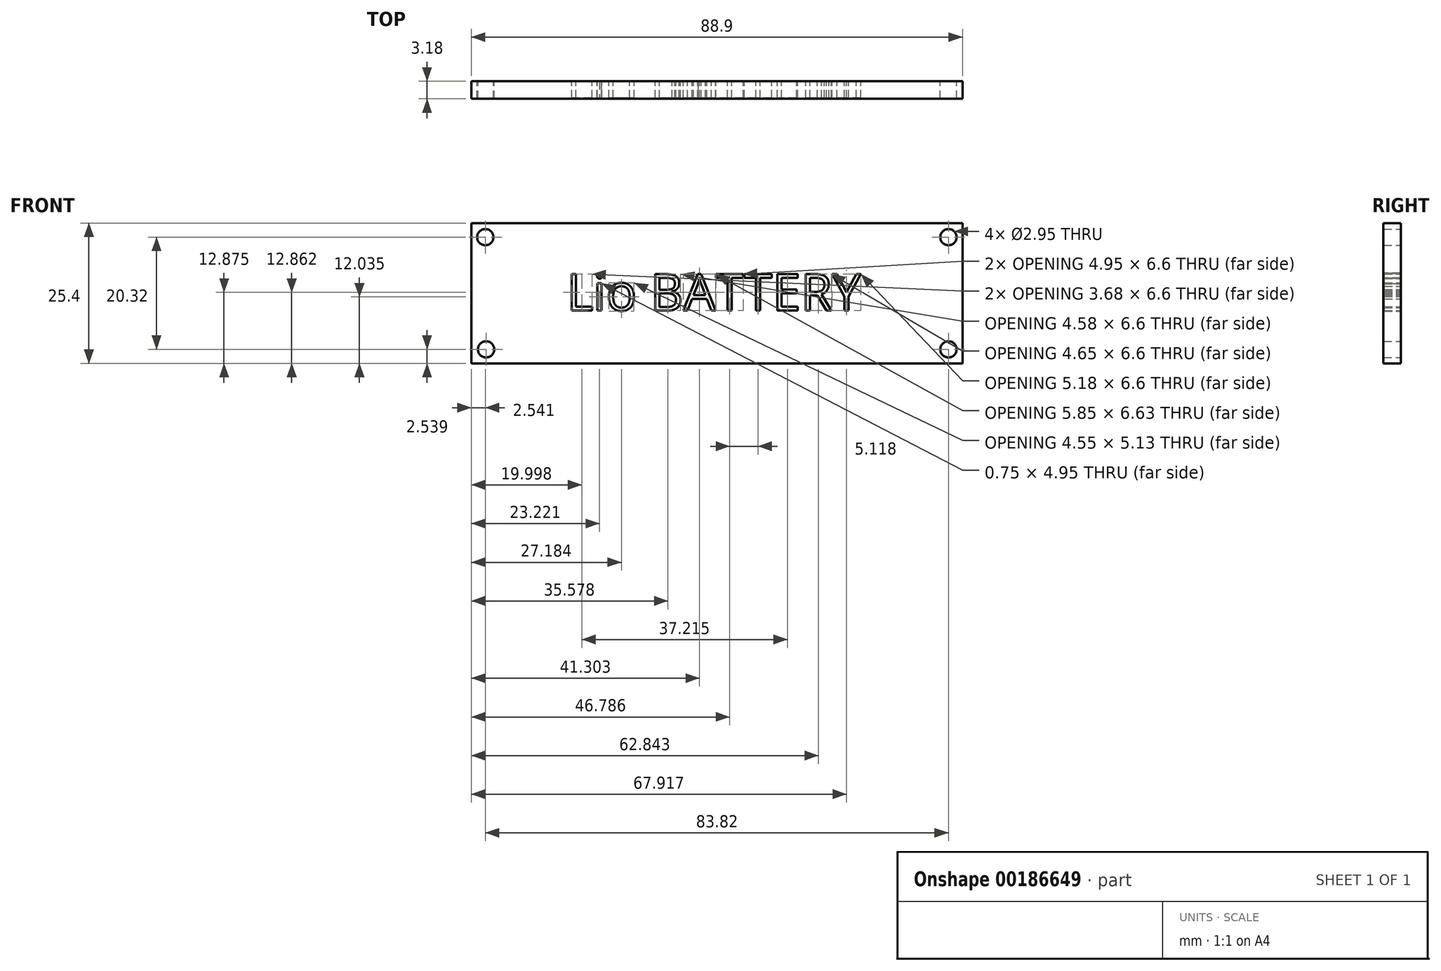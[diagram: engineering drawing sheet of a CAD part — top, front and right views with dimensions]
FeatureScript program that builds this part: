
annotation { "Feature Type Name" : "Feature", "Feature Type Description" : "" }
export const myFeature = defineFeature(function(context is Context, id is Id, definition is map)
    precondition{}
    {
        {
            var Q0;
            Q0=qCreatedBy(makeId("Front.planeOp"),FACE);
            var sketch = newSketch(context, id + "F0", { "sketchPlane" : qUnion([Q0])});
            skLineSegment(sketch, "E0", {"start": v(-37, 26.19) * mm, "end": v(51.9, 26.19) * mm});
            skLineSegment(sketch, "E1", {"start": v(-37, 26.19) * mm, "end": v(-37, 0.79) * mm});
            skLineSegment(sketch, "E2", {"start": v(-37, 0.79) * mm, "end": v(51.9, 0.79) * mm});
            skLineSegment(sketch, "E3", {"start": v(51.9, 0.79) * mm, "end": v(51.9, 26.19) * mm});
            skCircle(sketch, "E4", {"center": v(-34.47, 23.65) * mm, "radius": 1.47 * mm});
            skCircle(sketch, "E5", {"center": v(-34.33, 3.33) * mm, "radius": 1.47 * mm});
            skCircle(sketch, "E6", {"center": v(49.35, 3.33) * mm, "radius": 1.47 * mm});
            skCircle(sketch, "E7", {"center": v(49.35, 23.65) * mm, "radius": 1.47 * mm});
            skText(sketch, "E8", { "text": "Lio BATTERY", "fontName": "OpenSans-Regular.ttf"});
            skLineSegment(sketch, "E9", {"start": v(51.9, 26.19) * mm, "end": v(-37, 0.79) * mm, "construction": true});
            skLineSegment(sketch, "E10", {"start": v(-37, 26.19) * mm, "end": v(51.9, 0.79) * mm, "construction": true});
            skLineSegment(sketch, "E11", {"start": v(-27.3, 26.19) * mm, "end": v(-27.3, 22.63) * mm, "construction": true});
            skLineSegment(sketch, "E12", {"start": v(-37, 18.2) * mm, "end": v(-33.45, 18.2) * mm, "construction": true});
            skLineSegment(sketch, "E13", {"start": v(-26.7, 0.79) * mm, "end": v(-26.7, 4.35) * mm, "construction": true});
            skLineSegment(sketch, "E14", {"start": v(51.9, 20.21) * mm, "end": v(48.34, 20.21) * mm, "construction": true});
            skLineSegment(sketch, "E15.top", {"start": v(-31.92, 2.35) * mm, "end": v(46.82, 2.35) * mm});
            skLineSegment(sketch, "E16.top", {"start": v(-35.41, 21.08) * mm, "end": v(-34.46, 21.08) * mm});
            skLineSegment(sketch, "E16.right", {"start": v(-31.92, 24.57) * mm, "end": v(-31.92, 23.62) * mm});
            skArc(sketch, "E17.filletArc", {"start": v(-34.46, 21.08) * mm, "mid": v(-32.66, 21.82) * mm, "end": v(-31.92, 23.62) * mm});
            skLineSegment(sketch, "E18.trimOffspring", {"start": v(-31.92, 24.57) * mm, "end": v(46.82, 24.57) * mm});
            skLineSegment(sketch, "E19.trimOffspring", {"start": v(-35.41, 21.08) * mm, "end": v(-35.41, 5.84) * mm});
            skLineSegment(sketch, "E20.top", {"start": v(50.31, 21.08) * mm, "end": v(49.36, 21.08) * mm});
            skLineSegment(sketch, "E20.right", {"start": v(46.82, 24.57) * mm, "end": v(46.82, 23.62) * mm});
            skArc(sketch, "E21.filletArc", {"start": v(46.82, 23.62) * mm, "mid": v(47.57, 21.82) * mm, "end": v(49.36, 21.08) * mm});
            skLineSegment(sketch, "E22.top", {"start": v(50.31, 5.84) * mm, "end": v(49.36, 5.84) * mm});
            skArc(sketch, "E23.filletArc", {"start": v(49.36, 5.84) * mm, "mid": v(47.6, 5.14) * mm, "end": v(46.82, 3.42) * mm});
            skLineSegment(sketch, "E24.top", {"start": v(-35.41, 5.84) * mm, "end": v(-34.46, 5.84) * mm});
            skLineSegment(sketch, "E24.right", {"start": v(-31.92, 2.35) * mm, "end": v(-31.92, 3.3) * mm});
            skArc(sketch, "E25.filletArc", {"start": v(-31.92, 3.3) * mm, "mid": v(-32.66, 5.1) * mm, "end": v(-34.46, 5.84) * mm});
            skLineSegment(sketch, "E26", {"start": v(-35.42, 19.5) * mm, "end": v(-37, 19.5) * mm, "construction": true});
            skLineSegment(sketch, "E27", {"start": v(46.82, 3.42) * mm, "end": v(46.82, 2.35) * mm});
            skLineSegment(sketch, "E28", {"start": v(46.82, 2.35) * mm, "end": v(46.82, 0.76) * mm, "construction": true});
            skLineSegment(sketch, "E29", {"start": v(50.31, 21.08) * mm, "end": v(50.31, 5.84) * mm});
            const initialGuessF0  = {"E8": [-0.01976, 0.01035, 1, 0, 0.00666]};
            skSetInitialGuess(sketch, initialGuessF0);
            skSolve(sketch);
        }
        {
            var Q0;
            Q0=makeQuery(id+"F0.imprint","IMPRINT",FACE,{"disambiguationData":[TD([[makeQuery(id+"F0.imprint","IMPRINT",EDGE,{"derivedFrom":sQuery(id+"F0.wireOp",EDGE,"E0")}),-1.0]])]});
            var Q1;
            Q1=makeQuery(id+"F0.imprint","IMPRINT",FACE,{"disambiguationData":[TD([[makeQuery(id+"F0.imprint","IMPRINT",EDGE,{"derivedFrom":sQuery(id+"F0.wireOp",EDGE,"E8.sketch_text.stroke-27")}),1.0]])]});
            var Q2;
            Q2=makeQuery(id+"F0.imprint","IMPRINT",FACE,{"disambiguationData":[TD([[makeQuery(id+"F0.imprint","IMPRINT",EDGE,{"derivedFrom":sQuery(id+"F0.wireOp",EDGE,"E8.sketch_text.stroke-46")}),1.0]])]});
            var Q3;
            Q3=makeQuery(id+"F0.imprint","IMPRINT",FACE,{"disambiguationData":[TD([[makeQuery(id+"F0.imprint","IMPRINT",EDGE,{"derivedFrom":sQuery(id+"F0.wireOp",EDGE,"E8.sketch_text.stroke-53")}),1.0]])]});
            var Q4;
            Q4=makeQuery(id+"F0.imprint","IMPRINT",FACE,{"disambiguationData":[TD([[makeQuery(id+"F0.imprint","IMPRINT",EDGE,{"derivedFrom":sQuery(id+"F0.wireOp",EDGE,"E8.sketch_text.stroke-68")}),1.0]])]});
            var Q5;
            Q5=makeQuery(id+"F0.imprint","IMPRINT",FACE,{"disambiguationData":[TD([[makeQuery(id+"F0.imprint","IMPRINT",EDGE,{"derivedFrom":sQuery(id+"F0.wireOp",EDGE,"E8.sketch_text.stroke-112")}),1.0]])]});
            var Q6;
            Q6=makeQuery(id+"F0.imprint","IMPRINT",FACE,{"disambiguationData":[TD([[makeQuery(id+"F0.imprint","IMPRINT",EDGE,{"derivedFrom":sQuery(id+"F0.wireOp",EDGE,"E8.sketch_text.stroke-0")}),1.0]])]});
            extrude(context, id + "F1", {"entities" : qUnion([Q0, Q1, Q2, Q3, Q4, Q5, Q6]), "depth" : 3.17 * mm});
        }
        {
            var Q0;
            Q0=makeQuery(id+"F0.imprint","IMPRINT",FACE,{"disambiguationData":[TD([[makeQuery(id+"F0.imprint","IMPRINT",EDGE,{"derivedFrom":sQuery(id+"F0.wireOp",EDGE,"E8.sketch_text.stroke-0")}),-1.0]])]});
            var Q1;
            Q1=makeQuery(id+"F0.imprint","IMPRINT",FACE,{"disambiguationData":[TD([[makeQuery(id+"F0.imprint","IMPRINT",EDGE,{"derivedFrom":sQuery(id+"F0.wireOp",EDGE,"E8.sketch_text.stroke-6")}),-1.0]])]});
            var Q2;
            Q2=makeQuery(id+"F0.imprint","IMPRINT",FACE,{"disambiguationData":[TD([[makeQuery(id+"F0.imprint","IMPRINT",EDGE,{"derivedFrom":sQuery(id+"F0.wireOp",EDGE,"E8.sketch_text.stroke-10")}),-1.0]])]});
            var Q3;
            Q3=makeQuery(id+"F0.imprint","IMPRINT",FACE,{"disambiguationData":[TD([[makeQuery(id+"F0.imprint","IMPRINT",EDGE,{"derivedFrom":sQuery(id+"F0.wireOp",EDGE,"E8.sketch_text.stroke-18")}),-1.0]])]});
            var Q4;
            Q4=makeQuery(id+"F0.imprint","IMPRINT",FACE,{"disambiguationData":[TD([[makeQuery(id+"F0.imprint","IMPRINT",EDGE,{"derivedFrom":sQuery(id+"F0.wireOp",EDGE,"E8.sketch_text.stroke-35")}),-1.0]])]});
            var Q5;
            Q5=makeQuery(id+"F0.imprint","IMPRINT",FACE,{"disambiguationData":[TD([[makeQuery(id+"F0.imprint","IMPRINT",EDGE,{"derivedFrom":sQuery(id+"F0.wireOp",EDGE,"E8.sketch_text.stroke-60")}),-1.0]])]});
            var Q6;
            Q6=makeQuery(id+"F0.imprint","IMPRINT",FACE,{"disambiguationData":[TD([[makeQuery(id+"F0.imprint","IMPRINT",EDGE,{"derivedFrom":sQuery(id+"F0.wireOp",EDGE,"E8.sketch_text.stroke-73")}),-1.0]])]});
            var Q7;
            Q7=makeQuery(id+"F0.imprint","IMPRINT",FACE,{"disambiguationData":[TD([[makeQuery(id+"F0.imprint","IMPRINT",EDGE,{"derivedFrom":sQuery(id+"F0.wireOp",EDGE,"E8.sketch_text.stroke-81")}),-1.0]])]});
            var Q8;
            Q8=makeQuery(id+"F0.imprint","IMPRINT",FACE,{"disambiguationData":[TD([[makeQuery(id+"F0.imprint","IMPRINT",EDGE,{"derivedFrom":sQuery(id+"F0.wireOp",EDGE,"E8.sketch_text.stroke-89")}),-1.0]])]});
            var Q9;
            Q9=makeQuery(id+"F0.imprint","IMPRINT",FACE,{"disambiguationData":[TD([[makeQuery(id+"F0.imprint","IMPRINT",EDGE,{"derivedFrom":sQuery(id+"F0.wireOp",EDGE,"E8.sketch_text.stroke-101")}),-1.0]])]});
            var Q10;
            Q10=makeQuery(id+"F0.imprint","IMPRINT",FACE,{"disambiguationData":[TD([[makeQuery(id+"F0.imprint","IMPRINT",EDGE,{"derivedFrom":sQuery(id+"F0.wireOp",EDGE,"E8.sketch_text.stroke-119")}),-1.0]])]});
            extrude(context, id + "F2", {"entities" : qUnion([Q0, Q1, Q2, Q3, Q4, Q5, Q6, Q7, Q8, Q9, Q10]), "depth" : 3.05 * mm});
        }
    });
